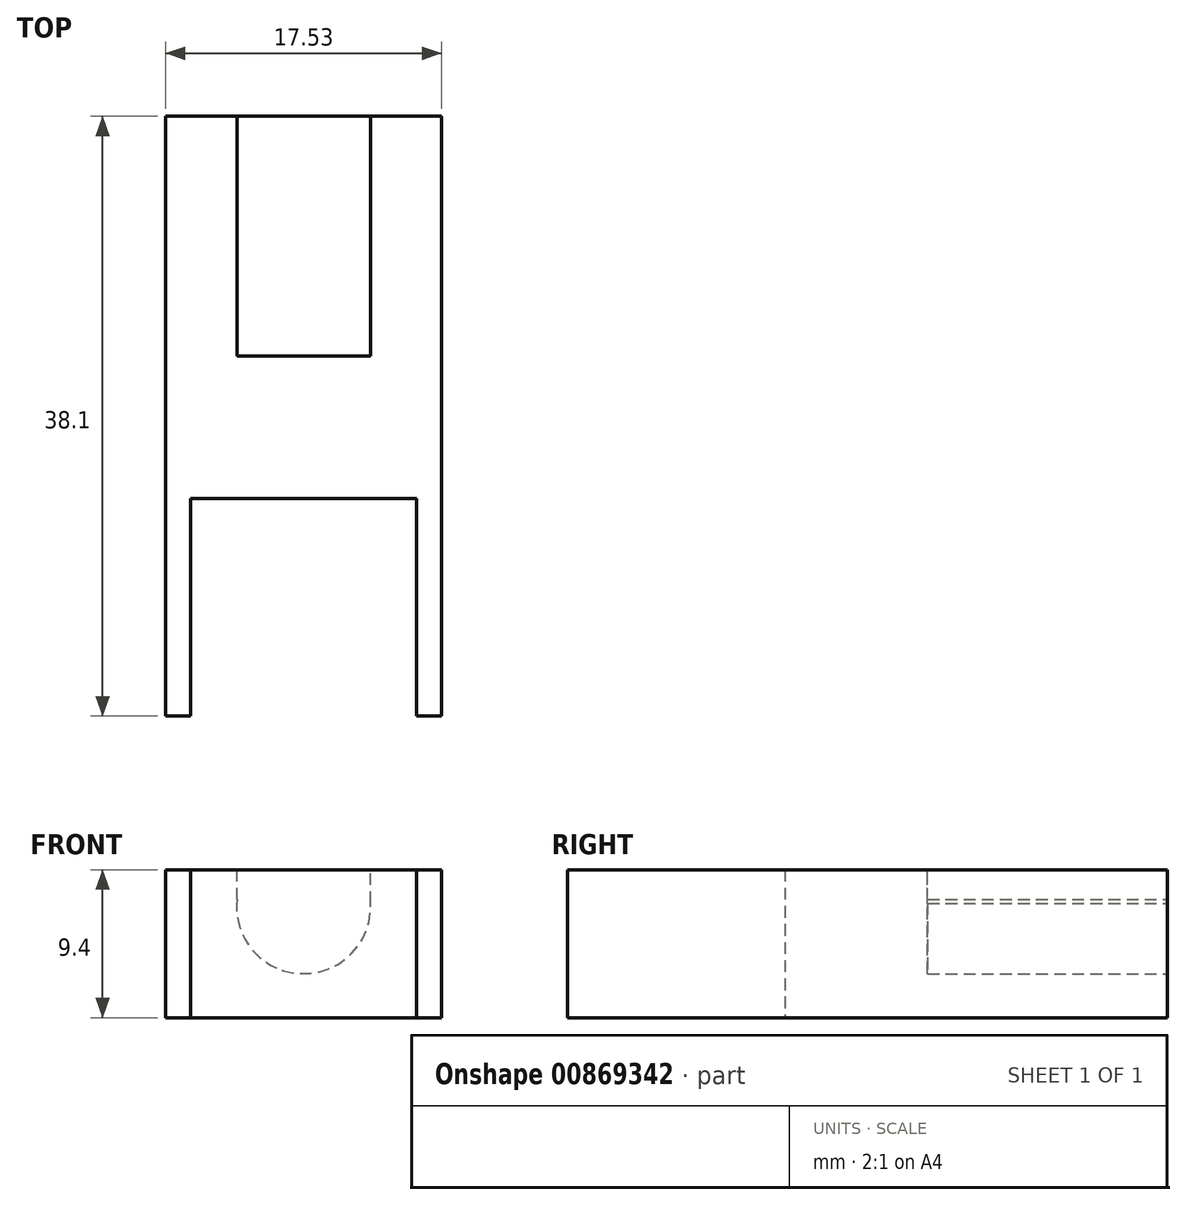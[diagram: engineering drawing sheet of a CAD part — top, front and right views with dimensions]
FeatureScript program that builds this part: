
annotation { "Feature Type Name" : "Feature", "Feature Type Description" : "" }
export const myFeature = defineFeature(function(context is Context, id is Id, definition is map)
    precondition{}
    {
        {
            var Q0;
            Q0=qCreatedBy(makeId("Top.planeOp"),FACE);
            var sketch = newSketch(context, id + "F0", { "sketchPlane" : qUnion([Q0])});
            skLineSegment(sketch, "E0.bottom", {"start": v(0, 0) * mm, "end": v(1.59, 0) * mm});
            skLineSegment(sketch, "E0.top", {"start": v(0, 38.1) * mm, "end": v(17.53, 38.1) * mm});
            skLineSegment(sketch, "E0.left", {"start": v(0, 0) * mm, "end": v(0, 38.1) * mm});
            skLineSegment(sketch, "E0.right", {"start": v(17.53, 0) * mm, "end": v(17.53, 38.1) * mm});
            skLineSegment(sketch, "E1.top", {"start": v(1.59, 13.82) * mm, "end": v(15.94, 13.82) * mm});
            skLineSegment(sketch, "E1.left", {"start": v(1.59, 0) * mm, "end": v(1.59, 13.82) * mm});
            skLineSegment(sketch, "E1.right", {"start": v(15.94, 0) * mm, "end": v(15.94, 13.82) * mm});
            skLineSegment(sketch, "E2.trimOffspring", {"start": v(15.94, 0) * mm, "end": v(17.53, 0) * mm});
            skLineSegment(sketch, "E3", {"start": v(1.59, 0) * mm, "end": v(15.94, 0) * mm});
            skSolve(sketch);
        }
        {
            var Q0;
            Q0=makeQuery(id+"F0.imprint","IMPRINT",FACE,{"disambiguationData":[TD([[makeQuery(id+"F0.imprint","IMPRINT",EDGE,{"derivedFrom":sQuery(id+"F0.wireOp",EDGE,"E0.bottom")}),1.0]])]});
            extrude(context, id + "F1", {"entities" : qUnion([Q0]), "depth" : 9.4 * mm, "offsetDistance" : 25.4 * mm});
        }
        {
            var Q0;
            Q0=makeQuery(id+"F1.opExtrude","SWEPT_FACE",FACE,{"disambiguationData":[OSD([sQuery(id+"F0.wireOp",EDGE,"E0.top")])]});
            var sketch = newSketch(context, id + "F2", { "sketchPlane" : qUnion([Q0])});
            skPoint(sketch, "E4.orphan", {"position": v(-8.76, 9.4) * mm});
            skPoint(sketch, "E5.start.orphan", {"position": v(-8.76, 4.7) * mm});
            skArc(sketch, "E6", {"start": v(-13, 7.27) * mm, "mid": v(-8.65, 2.8) * mm, "end": v(-4.53, 7.5) * mm});
            skLineSegment(sketch, "E7.top", {"start": v(-13, 11.37) * mm, "end": v(-4.53, 11.37) * mm});
            skLineSegment(sketch, "E7.left", {"start": v(-13, 7.27) * mm, "end": v(-13, 11.37) * mm});
            skLineSegment(sketch, "E7.right", {"start": v(-4.53, 7.27) * mm, "end": v(-4.53, 11.37) * mm});
            skSolve(sketch);
        }
        {
            var Q0;
            {var subQ0=sQuery(id+"F2.wireOp",EDGE,"E6");var subQ1=makeQuery(id+"F1.opExtrude","CAP_EDGE",EDGE,{"disambiguationData":[OSD([sQuery(id+"F0.wireOp",EDGE,"E0.top")])],"isStart":false});var subQ2=makeQuery(id+"F2.imprint","INTERSECT",VERTEX,{"disambiguationData":[OD(0.0)],"derivedFrom":[subQ1,subQ0]});Q0=makeQuery(id+"F2.imprint","IMPRINT",FACE,{"disambiguationData":[TD([[makeQuery(id+"F2.imprint","IMPRINT",EDGE,{"disambiguationData":[TD([[subQ2,1.0]])],"derivedFrom":subQ0}),1.0]])]});}
            extrude(context, id + "F3", {"entities" : qUnion([Q0]), "operationType" : NewBodyOperationType.REMOVE, "oppositeDirection" : true, "depth" : 15.24 * mm, "offsetDistance" : 25.4 * mm});
        }
    });
